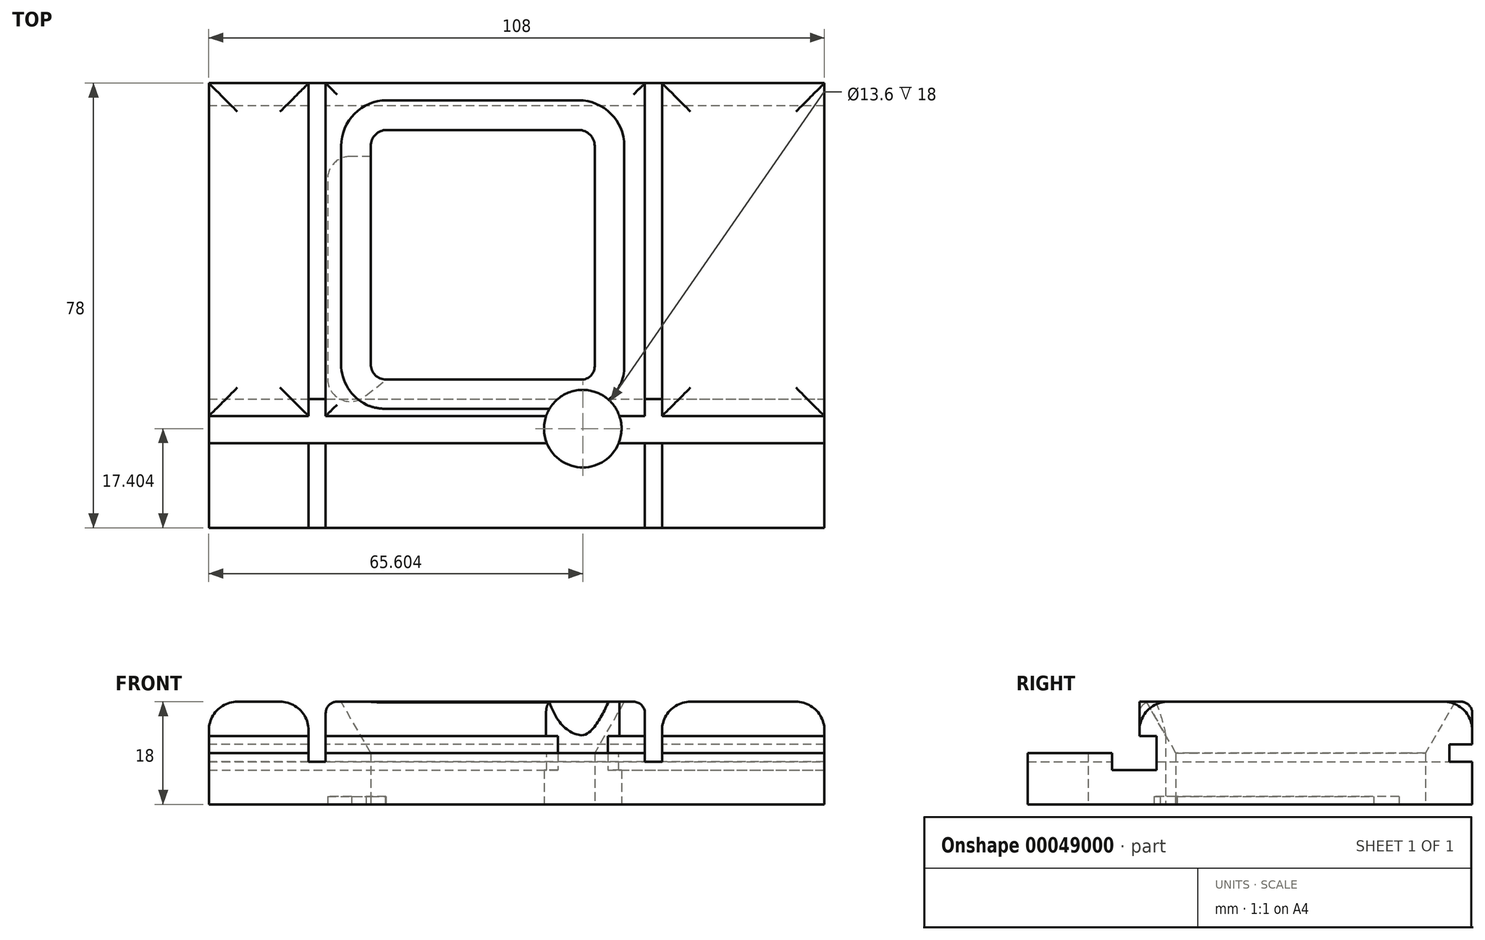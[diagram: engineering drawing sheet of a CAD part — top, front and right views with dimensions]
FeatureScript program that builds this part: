
annotation { "Feature Type Name" : "Feature", "Feature Type Description" : "" }
export const myFeature = defineFeature(function(context is Context, id is Id, definition is map)
    precondition{}
    {
        {
            var Q0;
            Q0=qCreatedBy(makeId("Top.planeOp"),FACE);
            var sketch = newSketch(context, id + "F0", { "sketchPlane" : qUnion([Q0])});
            skLineSegment(sketch, "E0.bottom", {"start": v(-52.02, 49.8) * mm, "end": v(55.98, 49.8) * mm});
            skLineSegment(sketch, "E0.top", {"start": v(-52.02, -28.2) * mm, "end": v(55.98, -28.2) * mm});
            skLineSegment(sketch, "E0.left", {"start": v(-52.02, 49.8) * mm, "end": v(-52.02, -28.2) * mm});
            skLineSegment(sketch, "E0.right", {"start": v(55.98, 49.8) * mm, "end": v(55.98, -28.2) * mm});
            skLineSegment(sketch, "E1", {"start": v(24.48, 49.8) * mm, "end": v(24.48, -28.2) * mm});
            skLineSegment(sketch, "E2", {"start": v(-34.52, 49.8) * mm, "end": v(-34.52, -28.2) * mm});
            skLineSegment(sketch, "E3", {"start": v(-31.52, 49.8) * mm, "end": v(-31.52, -28.2) * mm});
            skLineSegment(sketch, "E4", {"start": v(27.48, 49.8) * mm, "end": v(27.48, -28.2) * mm});
            skLineSegment(sketch, "E5", {"start": v(-52.02, -8.6) * mm, "end": v(55.98, -8.6) * mm});
            skLineSegment(sketch, "E6.bottom", {"start": v(-20.78, 41.6) * mm, "end": v(12.86, 41.6) * mm});
            skLineSegment(sketch, "E6.top", {"start": v(-20.9, -2.2) * mm, "end": v(13.36, -2.2) * mm});
            skLineSegment(sketch, "E6.left", {"start": v(-23.62, 38.77) * mm, "end": v(-23.62, 0.51) * mm});
            skLineSegment(sketch, "E6.right", {"start": v(15.68, 38.78) * mm, "end": v(15.68, 0.13) * mm});
            skCircle(sketch, "E7", {"center": v(13.58, -10.8) * mm, "radius": 6.8 * mm});
            skPoint(sketch, "E8.visualSharp", {"position": v(-23.62, 41.6) * mm});
            skArc(sketch, "E8.filletArc", {"start": v(-20.78, 41.6) * mm, "mid": v(-22.79, 40.77) * mm, "end": v(-23.62, 38.77) * mm});
            skPoint(sketch, "E9.visualSharp", {"position": v(15.68, 41.6) * mm});
            skArc(sketch, "E9.filletArc", {"start": v(15.68, 38.78) * mm, "mid": v(14.86, 40.78) * mm, "end": v(12.86, 41.6) * mm});
            skPoint(sketch, "E10.visualSharp", {"position": v(15.68, -2.2) * mm});
            skArc(sketch, "E10.filletArc", {"start": v(13.36, -2.2) * mm, "mid": v(15, -1.52) * mm, "end": v(15.68, 0.13) * mm});
            skPoint(sketch, "E11.visualSharp", {"position": v(-23.62, -2.2) * mm});
            skArc(sketch, "E11.filletArc", {"start": v(-23.62, 0.51) * mm, "mid": v(-22.82, -1.4) * mm, "end": v(-20.9, -2.2) * mm});
            skSolve(sketch);
        }
        {
            var Q0;
            {var subQ3=sQuery(id+"F0.wireOp",EDGE,"E1");var subQ5=sQuery(id+"F0.wireOp",EDGE,"E0.bottom");var subQ7=makeQuery(id+"F0.imprint","INTERSECT",VERTEX,{"derivedFrom":[subQ5,subQ3]});Q0=makeQuery(id+"F0.imprint","IMPRINT",FACE,{"disambiguationData":[TD([[makeQuery(id+"F0.imprint","IMPRINT",EDGE,{"disambiguationData":[TD([[subQ7,-1.0]])],"derivedFrom":subQ5}),-1.0]])]});}
            var Q1;
            {var subQ3=sQuery(id+"F0.wireOp",EDGE,"E2");var subQ5=sQuery(id+"F0.wireOp",EDGE,"E0.bottom");var subQ7=makeQuery(id+"F0.imprint","INTERSECT",VERTEX,{"derivedFrom":[subQ5,subQ3]});Q1=makeQuery(id+"F0.imprint","IMPRINT",FACE,{"disambiguationData":[TD([[makeQuery(id+"F0.imprint","IMPRINT",EDGE,{"disambiguationData":[TD([[subQ7,-1.0]])],"derivedFrom":subQ5}),-1.0]])]});}
            var Q2;
            {var subQ3=sQuery(id+"F0.wireOp",EDGE,"E0.left");var subQ5=sQuery(id+"F0.wireOp",EDGE,"E0.top");var subQ7=makeQuery(id+"F0.imprint","INTERSECT",VERTEX,{"derivedFrom":[subQ5,subQ3]});Q2=makeQuery(id+"F0.imprint","IMPRINT",FACE,{"disambiguationData":[TD([[makeQuery(id+"F0.imprint","IMPRINT",EDGE,{"disambiguationData":[TD([[subQ7,-1.0]])],"derivedFrom":subQ5}),1.0]])]});}
            var Q3;
            {var subQ3=sQuery(id+"F0.wireOp",EDGE,"E0.right");var subQ5=sQuery(id+"F0.wireOp",EDGE,"E0.top");var subQ7=makeQuery(id+"F0.imprint","INTERSECT",VERTEX,{"derivedFrom":[subQ5,subQ3]});Q3=makeQuery(id+"F0.imprint","IMPRINT",FACE,{"disambiguationData":[TD([[makeQuery(id+"F0.imprint","IMPRINT",EDGE,{"disambiguationData":[TD([[subQ7,1.0]])],"derivedFrom":subQ5}),1.0]])]});}
            var Q4;
            {var subQ3=sQuery(id+"F0.wireOp",EDGE,"E0.left");var subQ5=sQuery(id+"F0.wireOp",EDGE,"E0.bottom");var subQ7=makeQuery(id+"F0.imprint","INTERSECT",VERTEX,{"derivedFrom":[subQ5,subQ3]});Q4=makeQuery(id+"F0.imprint","IMPRINT",FACE,{"disambiguationData":[TD([[makeQuery(id+"F0.imprint","IMPRINT",EDGE,{"disambiguationData":[TD([[subQ7,-1.0]])],"derivedFrom":subQ5}),-1.0]])]});}
            var Q5;
            {var subQ3=sQuery(id+"F0.wireOp",EDGE,"E0.right");var subQ5=sQuery(id+"F0.wireOp",EDGE,"E0.bottom");var subQ7=makeQuery(id+"F0.imprint","INTERSECT",VERTEX,{"derivedFrom":[subQ5,subQ3]});Q5=makeQuery(id+"F0.imprint","IMPRINT",FACE,{"disambiguationData":[TD([[makeQuery(id+"F0.imprint","IMPRINT",EDGE,{"disambiguationData":[TD([[subQ7,1.0]])],"derivedFrom":subQ5}),-1.0]])]});}
            var Q6;
            Q6=makeQuery(id+"F0.imprint","IMPRINT",FACE,{"disambiguationData":[TD([[makeQuery(id+"F0.imprint","IMPRINT",EDGE,{"derivedFrom":sQuery(id+"F0.wireOp",EDGE,"E6.bottom")}),1.0]])]});
            var Q7;
            {var subQ4=sQuery(id+"F0.wireOp",EDGE,"E1");var subQ8=sQuery(id+"F0.wireOp",EDGE,"E0.top");var subQ10=makeQuery(id+"F0.imprint","INTERSECT",VERTEX,{"derivedFrom":[subQ8,subQ4]});Q7=makeQuery(id+"F0.imprint","IMPRINT",FACE,{"disambiguationData":[TD([[makeQuery(id+"F0.imprint","IMPRINT",EDGE,{"disambiguationData":[TD([[subQ10,1.0]])],"derivedFrom":subQ8}),1.0]])]});}
            var Q8;
            {var subQ3=sQuery(id+"F0.wireOp",EDGE,"E1");var subQ5=sQuery(id+"F0.wireOp",EDGE,"E0.top");var subQ7=makeQuery(id+"F0.imprint","INTERSECT",VERTEX,{"derivedFrom":[subQ5,subQ3]});Q8=makeQuery(id+"F0.imprint","IMPRINT",FACE,{"disambiguationData":[TD([[makeQuery(id+"F0.imprint","IMPRINT",EDGE,{"disambiguationData":[TD([[subQ7,-1.0]])],"derivedFrom":subQ5}),1.0]])]});}
            var Q9;
            {var subQ3=sQuery(id+"F0.wireOp",EDGE,"E2");var subQ5=sQuery(id+"F0.wireOp",EDGE,"E0.top");var subQ7=makeQuery(id+"F0.imprint","INTERSECT",VERTEX,{"derivedFrom":[subQ5,subQ3]});Q9=makeQuery(id+"F0.imprint","IMPRINT",FACE,{"disambiguationData":[TD([[makeQuery(id+"F0.imprint","IMPRINT",EDGE,{"disambiguationData":[TD([[subQ7,-1.0]])],"derivedFrom":subQ5}),1.0]])]});}
            extrude(context, id + "F1", {"entities" : qUnion([Q0, Q1, Q2, Q3, Q4, Q5, Q6, Q7, Q8, Q9]), "depth" : 7.5 * mm});
        }
        {
            var Q0;
            {var subQ3=sQuery(id+"F0.wireOp",EDGE,"E0.left");var subQ5=sQuery(id+"F0.wireOp",EDGE,"E0.bottom");var subQ7=makeQuery(id+"F0.imprint","INTERSECT",VERTEX,{"derivedFrom":[subQ5,subQ3]});Q0=makeQuery(id+"F0.imprint","IMPRINT",FACE,{"disambiguationData":[TD([[makeQuery(id+"F0.imprint","IMPRINT",EDGE,{"disambiguationData":[TD([[subQ7,-1.0]])],"derivedFrom":subQ5}),-1.0]])]});}
            var Q1;
            {var subQ3=sQuery(id+"F0.wireOp",EDGE,"E0.left");var subQ5=sQuery(id+"F0.wireOp",EDGE,"E0.top");var subQ7=makeQuery(id+"F0.imprint","INTERSECT",VERTEX,{"derivedFrom":[subQ5,subQ3]});Q1=makeQuery(id+"F0.imprint","IMPRINT",FACE,{"disambiguationData":[TD([[makeQuery(id+"F0.imprint","IMPRINT",EDGE,{"disambiguationData":[TD([[subQ7,-1.0]])],"derivedFrom":subQ5}),1.0]])]});}
            var Q2;
            {var subQ4=sQuery(id+"F0.wireOp",EDGE,"E1");var subQ8=sQuery(id+"F0.wireOp",EDGE,"E0.top");var subQ10=makeQuery(id+"F0.imprint","INTERSECT",VERTEX,{"derivedFrom":[subQ8,subQ4]});Q2=makeQuery(id+"F0.imprint","IMPRINT",FACE,{"disambiguationData":[TD([[makeQuery(id+"F0.imprint","IMPRINT",EDGE,{"disambiguationData":[TD([[subQ10,1.0]])],"derivedFrom":subQ8}),1.0]])]});}
            var Q3;
            Q3=makeQuery(id+"F0.imprint","IMPRINT",FACE,{"disambiguationData":[TD([[makeQuery(id+"F0.imprint","IMPRINT",EDGE,{"derivedFrom":sQuery(id+"F0.wireOp",EDGE,"E6.bottom")}),1.0]])]});
            var Q4;
            {var subQ3=sQuery(id+"F0.wireOp",EDGE,"E0.right");var subQ5=sQuery(id+"F0.wireOp",EDGE,"E0.bottom");var subQ7=makeQuery(id+"F0.imprint","INTERSECT",VERTEX,{"derivedFrom":[subQ5,subQ3]});Q4=makeQuery(id+"F0.imprint","IMPRINT",FACE,{"disambiguationData":[TD([[makeQuery(id+"F0.imprint","IMPRINT",EDGE,{"disambiguationData":[TD([[subQ7,1.0]])],"derivedFrom":subQ5}),-1.0]])]});}
            var Q5;
            {var subQ3=sQuery(id+"F0.wireOp",EDGE,"E0.right");var subQ5=sQuery(id+"F0.wireOp",EDGE,"E0.top");var subQ7=makeQuery(id+"F0.imprint","INTERSECT",VERTEX,{"derivedFrom":[subQ5,subQ3]});Q5=makeQuery(id+"F0.imprint","IMPRINT",FACE,{"disambiguationData":[TD([[makeQuery(id+"F0.imprint","IMPRINT",EDGE,{"disambiguationData":[TD([[subQ7,1.0]])],"derivedFrom":subQ5}),1.0]])]});}
            extrude(context, id + "F2", {"entities" : qUnion([Q0, Q1, Q2, Q3, Q4, Q5]), "operationType" : NewBodyOperationType.ADD, "depth" : 9 * mm});
        }
        {
            var Q0;
            {var subQ3=sQuery(id+"F0.wireOp",EDGE,"E0.left");var subQ5=sQuery(id+"F0.wireOp",EDGE,"E0.bottom");var subQ7=makeQuery(id+"F0.imprint","INTERSECT",VERTEX,{"derivedFrom":[subQ5,subQ3]});Q0=makeQuery(id+"F0.imprint","IMPRINT",FACE,{"disambiguationData":[TD([[makeQuery(id+"F0.imprint","IMPRINT",EDGE,{"disambiguationData":[TD([[subQ7,-1.0]])],"derivedFrom":subQ5}),-1.0]])]});}
            var Q1;
            Q1=makeQuery(id+"F0.imprint","IMPRINT",FACE,{"disambiguationData":[TD([[makeQuery(id+"F0.imprint","IMPRINT",EDGE,{"derivedFrom":sQuery(id+"F0.wireOp",EDGE,"E6.bottom")}),1.0]])]});
            var Q2;
            {var subQ3=sQuery(id+"F0.wireOp",EDGE,"E0.right");var subQ5=sQuery(id+"F0.wireOp",EDGE,"E0.bottom");var subQ7=makeQuery(id+"F0.imprint","INTERSECT",VERTEX,{"derivedFrom":[subQ5,subQ3]});Q2=makeQuery(id+"F0.imprint","IMPRINT",FACE,{"disambiguationData":[TD([[makeQuery(id+"F0.imprint","IMPRINT",EDGE,{"disambiguationData":[TD([[subQ7,1.0]])],"derivedFrom":subQ5}),-1.0]])]});}
            extrude(context, id + "F3", {"entities" : qUnion([Q0, Q1, Q2]), "operationType" : NewBodyOperationType.ADD, "depth" : 18 * mm});
        }
        {
            var Q0;
            Q0=makeQuery(id+"F3.opExtrude","CAP_FACE",FACE,{"disambiguationData":[OSD([sQuery(id+"F0.wireOp",EDGE,"E0.bottom"),sQuery(id+"F0.wireOp",EDGE,"E0.right"),sQuery(id+"F0.wireOp",EDGE,"E4"),sQuery(id+"F0.wireOp",EDGE,"E5")])],"isStart":false});
            fillet(context, id + "F4", {"entities" : qUnion([Q0]), "radius" : 5 * mm, "tangentPropagation" : true, "allowEdgeOverflow" : false});
        }
        {
            var Q0;
            Q0=makeQuery(id+"F3.opExtrude","CAP_FACE",FACE,{"disambiguationData":[OSD([sQuery(id+"F0.wireOp",EDGE,"E0.bottom"),sQuery(id+"F0.wireOp",EDGE,"E0.left"),sQuery(id+"F0.wireOp",EDGE,"E2"),sQuery(id+"F0.wireOp",EDGE,"E5")])],"isStart":false});
            fillet(context, id + "F5", {"entities" : qUnion([Q0]), "radius" : 5 * mm, "tangentPropagation" : true, "allowEdgeOverflow" : false});
        }
        {
            var Q0;
            Q0=makeQuery(id+"F3.opExtrude","CAP_EDGE",EDGE,{"disambiguationData":[OSD([sQuery(id+"F0.wireOp",EDGE,"E6.left")])],"isStart":false});
            var Q1;
            Q1=makeQuery(id+"F3.opExtrude","CAP_EDGE",EDGE,{"disambiguationData":[OSD([sQuery(id+"F0.wireOp",EDGE,"E6.bottom")])],"isStart":false});
            var Q2;
            Q2=makeQuery(id+"F3.opExtrude","CAP_EDGE",EDGE,{"disambiguationData":[OSD([sQuery(id+"F0.wireOp",EDGE,"E6.right")])],"isStart":false});
            var Q3;
            Q3=makeQuery(id+"F3.opExtrude","CAP_EDGE",EDGE,{"disambiguationData":[OSD([sQuery(id+"F0.wireOp",EDGE,"E6.top")])],"isStart":false});
            chamfer(context, id + "F6", {"entities" : qUnion([Q0, Q1, Q2, Q3]), "chamferType" : ChamferType.OFFSET_ANGLE, "width" : 9 * mm, "oppositeDirection" : false, "angle" : 30 * degree, "tangentPropagation" : true});
        }
        {
            var Q0;
            Q0=makeQuery(id+"F3.opExtrude","CAP_EDGE",EDGE,{"disambiguationData":[OSD([sQuery(id+"F0.wireOp",EDGE,"E3")])],"isStart":false});
            var Q1;
            {var subQ0=sQuery(id+"F0.wireOp",EDGE,"E0.bottom");Q1=makeQuery(id+"F3.opExtrude","CAP_EDGE",EDGE,{"disambiguationData":[OSD([subQ0]),TDD([makeQuery(id+"F0.imprint","IMPRINT",EDGE,{"disambiguationData":[TD([[makeQuery(id+"F0.imprint","INTERSECT",VERTEX,{"derivedFrom":[subQ0,sQuery(id+"F0.wireOp",EDGE,"E1")]}),1.0]])],"derivedFrom":subQ0})])],"isStart":false});}
            var Q2;
            Q2=makeQuery(id+"F3.opExtrude","CAP_EDGE",EDGE,{"disambiguationData":[OSD([sQuery(id+"F0.wireOp",EDGE,"E1")])],"isStart":false});
            var Q3;
            {var subQ0=sQuery(id+"F0.wireOp",EDGE,"E5");Q3=makeQuery(id+"F3.opExtrude","CAP_EDGE",EDGE,{"disambiguationData":[OSD([subQ0]),TDD([makeQuery(id+"F0.imprint","IMPRINT",EDGE,{"disambiguationData":[TD([[makeQuery(id+"F0.imprint","INTERSECT",VERTEX,{"derivedFrom":[sQuery(id+"F0.wireOp",EDGE,"E3"),subQ0]}),-1.0]])],"derivedFrom":subQ0})])],"isStart":false});}
            fillet(context, id + "F7", {"entities" : qUnion([Q0, Q1, Q2, Q3]), "radius" : 2 * mm, "tangentPropagation" : true, "allowEdgeOverflow" : false});
        }
        {
            var Q0;
            {var subQ0=sQuery(id+"F0.wireOp",EDGE,"E0.bottom");var subQ1=makeQuery(id+"F0.imprint","IMPRINT",EDGE,{"disambiguationData":[TD([[makeQuery(id+"F0.imprint","INTERSECT",VERTEX,{"derivedFrom":[subQ0,sQuery(id+"F0.wireOp",EDGE,"E0.left")]}),-1.0]])],"derivedFrom":subQ0});var subQ2=makeQuery(id+"F0.imprint","IMPRINT",EDGE,{"disambiguationData":[TD([[makeQuery(id+"F0.imprint","INTERSECT",VERTEX,{"derivedFrom":[subQ0,sQuery(id+"F0.wireOp",EDGE,"E1")]}),1.0]])],"derivedFrom":subQ0});var subQ3=makeQuery(id+"F0.imprint","IMPRINT",EDGE,{"disambiguationData":[TD([[makeQuery(id+"F0.imprint","INTERSECT",VERTEX,{"derivedFrom":[subQ0,sQuery(id+"F0.wireOp",EDGE,"E0.right")]}),1.0]])],"derivedFrom":subQ0});Q0=makeQuery(id+"F3.boolean.opBoolean","MERGE",FACE,{"derivedFrom":[makeQuery(id+"F2.boolean.opBoolean","MERGE",FACE,{"derivedFrom":[makeQuery(id+"F1.opExtrude","SWEPT_FACE",FACE,{"disambiguationData":[OSD([subQ0])]}),makeQuery(id+"F2.opExtrude","SWEPT_FACE",FACE,{"disambiguationData":[OSD([subQ0]),TDD([subQ1])]}),makeQuery(id+"F2.opExtrude","SWEPT_FACE",FACE,{"disambiguationData":[OSD([subQ0]),TDD([subQ2])]}),makeQuery(id+"F2.opExtrude","SWEPT_FACE",FACE,{"disambiguationData":[OSD([subQ0]),TDD([subQ3])]})]}),makeQuery(id+"F3.opExtrude","SWEPT_FACE",FACE,{"disambiguationData":[OSD([subQ0]),TDD([subQ1])]}),makeQuery(id+"F3.opExtrude","SWEPT_FACE",FACE,{"disambiguationData":[OSD([subQ0]),TDD([subQ2])]}),makeQuery(id+"F3.opExtrude","SWEPT_FACE",FACE,{"disambiguationData":[OSD([subQ0]),TDD([subQ3])]})]});}
            var sketch = newSketch(context, id + "F8", { "sketchPlane" : qUnion([Q0])});
            skLineSegment(sketch, "E12.bottom", {"start": v(-55.98, 7.5) * mm, "end": v(52.02, 7.5) * mm});
            skLineSegment(sketch, "E12.top", {"start": v(-55.98, 10.5) * mm, "end": v(52.02, 10.5) * mm});
            skLineSegment(sketch, "E12.left", {"start": v(-55.98, 7.5) * mm, "end": v(-55.98, 10.5) * mm});
            skLineSegment(sketch, "E12.right", {"start": v(52.02, 7.5) * mm, "end": v(52.02, 10.5) * mm});
            skSolve(sketch);
        }
        {
            var Q0;
            {var subQ0=sQuery(id+"F0.wireOp",EDGE,"E0.bottom");var subQ1=sQuery(id+"F0.wireOp",EDGE,"E3");var subQ2=makeQuery(id+"F3.boolean.opBoolean","MERGE",EDGE,{"derivedFrom":[makeQuery(id+"F2.opExtrude","SWEPT_EDGE",EDGE,{"disambiguationData":[OSD([subQ0,subQ1])]}),makeQuery(id+"F3.opExtrude","SWEPT_EDGE",EDGE,{"disambiguationData":[OSD([subQ0,subQ1])]})]});var subQ5=sQuery(id+"F8.wireOp",EDGE,"E12.bottom");var subQ6=makeQuery(id+"F8.imprint","INTERSECT",VERTEX,{"derivedFrom":[subQ2,subQ5]});var subQ7=sQuery(id+"F0.wireOp",EDGE,"E1");var subQ8=makeQuery(id+"F3.boolean.opBoolean","MERGE",EDGE,{"derivedFrom":[makeQuery(id+"F2.opExtrude","SWEPT_EDGE",EDGE,{"disambiguationData":[OSD([subQ0,subQ7])]}),makeQuery(id+"F3.opExtrude","SWEPT_EDGE",EDGE,{"disambiguationData":[OSD([subQ0,subQ7])]})]});var subQ10=makeQuery(id+"F8.imprint","INTERSECT",VERTEX,{"derivedFrom":[subQ8,subQ5]});Q0=makeQuery(id+"F8.imprint","IMPRINT",FACE,{"disambiguationData":[TD([[makeQuery(id+"F8.imprint","IMPRINT",EDGE,{"disambiguationData":[TD([[subQ10,-1.0],[subQ6,1.0]])],"derivedFrom":subQ5}),1.0]])]});}
            var Q1;
            {var subQ7=sQuery(id+"F8.wireOp",EDGE,"E12.left");Q1=makeQuery(id+"F8.imprint","IMPRINT",FACE,{"disambiguationData":[TD([[makeQuery(id+"F8.imprint","IMPRINT",EDGE,{"derivedFrom":subQ7}),1.0]])]});}
            var Q2;
            {var subQ7=sQuery(id+"F8.wireOp",EDGE,"E12.right");Q2=makeQuery(id+"F8.imprint","IMPRINT",FACE,{"disambiguationData":[TD([[makeQuery(id+"F8.imprint","IMPRINT",EDGE,{"derivedFrom":subQ7}),-1.0]])]});}
            extrude(context, id + "F9", {"entities" : qUnion([Q0, Q1, Q2]), "operationType" : NewBodyOperationType.REMOVE, "oppositeDirection" : true, "depth" : 4 * mm});
        }
        {
            var Q0;
            {var subQ0=sQuery(id+"F0.wireOp",EDGE,"E5");Q0=makeQuery(id+"F3.opExtrude","SWEPT_FACE",FACE,{"disambiguationData":[OSD([subQ0]),TDD([makeQuery(id+"F0.imprint","IMPRINT",EDGE,{"disambiguationData":[TD([[makeQuery(id+"F0.imprint","INTERSECT",VERTEX,{"derivedFrom":[sQuery(id+"F0.wireOp",EDGE,"E3"),subQ0]}),-1.0]])],"derivedFrom":subQ0})])]});}
            var sketch = newSketch(context, id + "F10", { "sketchPlane" : qUnion([Q0])});
            skLineSegment(sketch, "E13.bottom", {"start": v(-52.82, 9) * mm, "end": v(58.8, 9) * mm});
            skLineSegment(sketch, "E13.top", {"start": v(-52.82, 12) * mm, "end": v(58.8, 12) * mm});
            skLineSegment(sketch, "E13.left", {"start": v(-52.82, 9) * mm, "end": v(-52.82, 12) * mm});
            skLineSegment(sketch, "E13.right", {"start": v(58.8, 9) * mm, "end": v(58.8, 12) * mm});
            skSolve(sketch);
        }
        {
            var Q0;
            {var subQ5=sQuery(id+"F10.wireOp",EDGE,"E13.left");Q0=makeQuery(id+"F10.imprint","IMPRINT",FACE,{"disambiguationData":[TD([[makeQuery(id+"F10.imprint","IMPRINT",EDGE,{"derivedFrom":subQ5}),-1.0]])]});}
            var Q1;
            {var subQ0=sQuery(id+"F0.wireOp",EDGE,"E5");var subQ1=sQuery(id+"F0.wireOp",EDGE,"E7");var subQ2=makeQuery(id+"F3.opExtrude","SWEPT_EDGE",EDGE,{"disambiguationData":[OSD([subQ0,subQ1]),TDD([makeQuery(id+"F0.imprint","INTERSECT",VERTEX,{"disambiguationData":[OD(0.0)],"derivedFrom":[subQ0,subQ1]})])]});var subQ5=sQuery(id+"F10.wireOp",EDGE,"E13.bottom");var subQ6=makeQuery(id+"F10.imprint","INTERSECT",VERTEX,{"derivedFrom":[subQ2,subQ5]});var subQ7=makeQuery(id+"F3.opExtrude","SWEPT_EDGE",EDGE,{"disambiguationData":[OSD([sQuery(id+"F0.wireOp",EDGE,"E3"),subQ0])]});var subQ9=makeQuery(id+"F10.imprint","INTERSECT",VERTEX,{"derivedFrom":[subQ7,subQ5]});Q1=makeQuery(id+"F10.imprint","IMPRINT",FACE,{"disambiguationData":[TD([[makeQuery(id+"F10.imprint","IMPRINT",EDGE,{"disambiguationData":[TD([[subQ9,1.0],[subQ6,-1.0]])],"derivedFrom":subQ5}),-1.0]])]});}
            var Q2;
            {var subQ7=sQuery(id+"F10.wireOp",EDGE,"E13.right");Q2=makeQuery(id+"F10.imprint","IMPRINT",FACE,{"disambiguationData":[TD([[makeQuery(id+"F10.imprint","IMPRINT",EDGE,{"derivedFrom":subQ7}),1.0]])]});}
            extrude(context, id + "F11", {"entities" : qUnion([Q0, Q1, Q2]), "operationType" : NewBodyOperationType.REMOVE, "oppositeDirection" : true, "depth" : 3 * mm});
        }
        {
            var Q0;
            Q0=makeQuery(id+"F11.boolean.opBoolean","MERGE",FACE,{"derivedFrom":[makeQuery(id+"F2.opExtrude","CAP_FACE",FACE,{"disambiguationData":[OSD([sQuery(id+"F0.wireOp",EDGE,"E0.bottom"),sQuery(id+"F0.wireOp",EDGE,"E0.top"),sQuery(id+"F0.wireOp",EDGE,"E1"),sQuery(id+"F0.wireOp",EDGE,"E3"),sQuery(id+"F0.wireOp",EDGE,"E6.bottom"),sQuery(id+"F0.wireOp",EDGE,"E6.top"),sQuery(id+"F0.wireOp",EDGE,"E6.left"),sQuery(id+"F0.wireOp",EDGE,"E6.right"),sQuery(id+"F0.wireOp",EDGE,"E7"),sQuery(id+"F0.wireOp",EDGE,"E8.filletArc"),sQuery(id+"F0.wireOp",EDGE,"E9.filletArc"),sQuery(id+"F0.wireOp",EDGE,"E10.filletArc"),sQuery(id+"F0.wireOp",EDGE,"E11.filletArc")])],"isStart":false}),makeQuery(id+"F11.opExtrude","SWEPT_FACE",FACE,{"disambiguationData":[OSD([sQuery(id+"F10.wireOp",EDGE,"E13.bottom")])]})]});
            var sketch = newSketch(context, id + "F12", { "sketchPlane" : qUnion([Q0])});
            skLineSegment(sketch, "E14.bottom", {"start": v(-60.93, -5.6) * mm, "end": v(56.85, -5.6) * mm});
            skLineSegment(sketch, "E14.top", {"start": v(-60.93, -13.37) * mm, "end": v(56.85, -13.37) * mm});
            skLineSegment(sketch, "E14.left", {"start": v(-60.93, -5.6) * mm, "end": v(-60.93, -13.37) * mm});
            skLineSegment(sketch, "E14.right", {"start": v(56.85, -5.6) * mm, "end": v(56.85, -13.37) * mm});
            skSolve(sketch);
        }
        {
            var Q0;
            {var subQ1=makeQuery(id+"F11.opExtrude","SWEPT_FACE",FACE,{"disambiguationData":[OSD([sQuery(id+"F10.wireOp",EDGE,"E13.bottom")])]});var subQ5=sQuery(id+"F12.wireOp",EDGE,"E14.bottom");var subQ7=sQuery(id+"F0.wireOp",EDGE,"E3");var subQ8=makeQuery(id+"F11.boolean.opBoolean","INTERSECT",EDGE,{"derivedFrom":[makeQuery(id+"F3.boolean.opBoolean","MERGE",FACE,{"derivedFrom":[makeQuery(id+"F2.opExtrude","SWEPT_FACE",FACE,{"disambiguationData":[OSD([subQ7])]}),makeQuery(id+"F3.opExtrude","SWEPT_FACE",FACE,{"disambiguationData":[OSD([subQ7])]})]}),subQ1]});var subQ10=makeQuery(id+"F12.imprint","INTERSECT",VERTEX,{"derivedFrom":[subQ8,subQ5]});Q0=makeQuery(id+"F12.imprint","IMPRINT",FACE,{"disambiguationData":[TD([[makeQuery(id+"F12.imprint","IMPRINT",EDGE,{"disambiguationData":[TD([[subQ10,-1.0]])],"derivedFrom":subQ5}),-1.0]])]});}
            var Q1;
            {var subQ6=sQuery(id+"F12.wireOp",EDGE,"E14.left");Q1=makeQuery(id+"F12.imprint","IMPRINT",FACE,{"disambiguationData":[TD([[makeQuery(id+"F12.imprint","IMPRINT",EDGE,{"derivedFrom":subQ6}),1.0]])]});}
            var Q2;
            {var subQ1=makeQuery(id+"F11.opExtrude","SWEPT_FACE",FACE,{"disambiguationData":[OSD([sQuery(id+"F10.wireOp",EDGE,"E13.bottom")])]});var subQ5=sQuery(id+"F12.wireOp",EDGE,"E14.bottom");var subQ7=sQuery(id+"F0.wireOp",EDGE,"E1");var subQ8=makeQuery(id+"F11.boolean.opBoolean","INTERSECT",EDGE,{"derivedFrom":[makeQuery(id+"F3.boolean.opBoolean","MERGE",FACE,{"derivedFrom":[makeQuery(id+"F2.opExtrude","SWEPT_FACE",FACE,{"disambiguationData":[OSD([subQ7])]}),makeQuery(id+"F3.opExtrude","SWEPT_FACE",FACE,{"disambiguationData":[OSD([subQ7])]})]}),subQ1]});var subQ10=makeQuery(id+"F12.imprint","INTERSECT",VERTEX,{"derivedFrom":[subQ8,subQ5]});Q2=makeQuery(id+"F12.imprint","IMPRINT",FACE,{"disambiguationData":[TD([[makeQuery(id+"F12.imprint","IMPRINT",EDGE,{"disambiguationData":[TD([[subQ10,1.0]])],"derivedFrom":subQ5}),-1.0]])]});}
            var Q3;
            {var subQ6=sQuery(id+"F12.wireOp",EDGE,"E14.right");Q3=makeQuery(id+"F12.imprint","IMPRINT",FACE,{"disambiguationData":[TD([[makeQuery(id+"F12.imprint","IMPRINT",EDGE,{"derivedFrom":subQ6}),-1.0]])]});}
            extrude(context, id + "F13", {"entities" : qUnion([Q0, Q1, Q2, Q3]), "operationType" : NewBodyOperationType.REMOVE, "oppositeDirection" : true, "depth" : 3 * mm});
        }
        {
            var Q0;
            Q0=makeQuery(id+"F0.imprint","IMPRINT",FACE,{"disambiguationData":[TD([[makeQuery(id+"F0.imprint","IMPRINT",EDGE,{"derivedFrom":sQuery(id+"F0.wireOp",EDGE,"E6.bottom")}),1.0]])]});
            var sketch = newSketch(context, id + "F14", { "sketchPlane" : qUnion([Q0])});
            skCircle(sketch, "E15", {"center": v(-27.18, -2.04) * mm, "radius": 4 * mm});
            skCircle(sketch, "E16", {"center": v(-27.18, 32.96) * mm, "radius": 4 * mm});
            skLineSegment(sketch, "E17.bottom", {"start": v(-31.18, -1.97) * mm, "end": v(-23.2, -1.97) * mm});
            skLineSegment(sketch, "E17.top", {"start": v(-31.18, 32.54) * mm, "end": v(-23.2, 32.54) * mm});
            skLineSegment(sketch, "E17.left", {"start": v(-31.18, -1.97) * mm, "end": v(-31.18, 32.54) * mm});
            skLineSegment(sketch, "E17.right", {"start": v(-23.2, -1.97) * mm, "end": v(-23.2, 32.54) * mm});
            skLineSegment(sketch, "E18", {"start": v(-20.95, -2.28) * mm, "end": v(-23.2, 0) * mm});
            skLineSegment(sketch, "E19", {"start": v(-26.98, 36.96) * mm, "end": v(-22.03, 36.96) * mm});
            skLineSegment(sketch, "E20", {"start": v(-22.03, 36.96) * mm, "end": v(-23.2, 32.54) * mm});
            skLineSegment(sketch, "E21", {"start": v(-20.95, -2.28) * mm, "end": v(-25.1, -5.45) * mm});
            skSolve(sketch);
        }
        {
            var Q0;
            {var subQ3=sQuery(id+"F14.wireOp",EDGE,"E17.bottom");Q0=makeQuery(id+"F14.imprint","IMPRINT",FACE,{"disambiguationData":[TD([[makeQuery(id+"F14.imprint","IMPRINT",EDGE,{"derivedFrom":subQ3}),-1.0]])]});}
            var Q1;
            {var subQ3=sQuery(id+"F14.wireOp",EDGE,"E17.bottom");Q1=makeQuery(id+"F14.imprint","IMPRINT",FACE,{"disambiguationData":[TD([[makeQuery(id+"F14.imprint","IMPRINT",EDGE,{"derivedFrom":subQ3}),1.0]])]});}
            var Q2;
            {var subQ9=sQuery(id+"F14.wireOp",EDGE,"E17.left");Q2=makeQuery(id+"F14.imprint","IMPRINT",FACE,{"disambiguationData":[TD([[makeQuery(id+"F14.imprint","IMPRINT",EDGE,{"derivedFrom":subQ9}),-1.0]])]});}
            var Q3;
            {var subQ1=sQuery(id+"F14.wireOp",EDGE,"E17.top");var subQ3=sQuery(id+"F14.wireOp",EDGE,"E16");var subQ5=makeQuery(id+"F14.imprint","INTERSECT",VERTEX,{"derivedFrom":[subQ3,subQ1]});Q3=makeQuery(id+"F14.imprint","IMPRINT",FACE,{"disambiguationData":[TD([[makeQuery(id+"F14.imprint","IMPRINT",EDGE,{"disambiguationData":[TD([[subQ5,-1.0]])],"derivedFrom":subQ3}),1.0]])]});}
            var Q4;
            {var subQ1=sQuery(id+"F14.wireOp",EDGE,"E17.top");var subQ3=sQuery(id+"F14.wireOp",EDGE,"E16");var subQ5=makeQuery(id+"F14.imprint","INTERSECT",VERTEX,{"derivedFrom":[subQ3,subQ1]});Q4=makeQuery(id+"F14.imprint","IMPRINT",FACE,{"disambiguationData":[TD([[makeQuery(id+"F14.imprint","IMPRINT",EDGE,{"disambiguationData":[TD([[subQ5,1.0]])],"derivedFrom":subQ3}),1.0]])]});}
            var Q5;
            {var subQ0=sQuery(id+"F14.wireOp",EDGE,"f461685c-614d-4517-aff4-d02b1853712a");var subQ1=sQuery(id+"F14.wireOp",EDGE,"E15");var subQ3=makeQuery(id+"F14.imprint","INTERSECT",VERTEX,{"disambiguationData":[OD(0.0)],"derivedFrom":[subQ1,subQ0]});Q5=makeQuery(id+"F14.imprint","IMPRINT",FACE,{"disambiguationData":[TD([[makeQuery(id+"F14.imprint","IMPRINT",EDGE,{"disambiguationData":[TD([[subQ3,-1.0]])],"derivedFrom":subQ1}),1.0]])]});}
            var Q6;
            {var subQ3=sQuery(id+"F14.wireOp",EDGE,"E17.right");var subQ7=sQuery(id+"F14.wireOp",EDGE,"E15");var subQ9=makeQuery(id+"F14.imprint","INTERSECT",VERTEX,{"derivedFrom":[subQ7,subQ3]});Q6=makeQuery(id+"F14.imprint","IMPRINT",FACE,{"disambiguationData":[TD([[makeQuery(id+"F14.imprint","IMPRINT",EDGE,{"disambiguationData":[TD([[subQ9,1.0]])],"derivedFrom":subQ7}),-1.0]])]});}
            var Q7;
            {var subQ1=sQuery(id+"F14.wireOp",EDGE,"E19");var subQ3=sQuery(id+"F14.wireOp",EDGE,"E16");var subQ5=makeQuery(id+"F14.imprint","INTERSECT",VERTEX,{"derivedFrom":[subQ3,subQ1]});Q7=makeQuery(id+"F14.imprint","IMPRINT",FACE,{"disambiguationData":[TD([[makeQuery(id+"F14.imprint","IMPRINT",EDGE,{"disambiguationData":[TD([[subQ5,1.0]])],"derivedFrom":subQ3}),-1.0]])]});}
            extrude(context, id + "F15", {"entities" : qUnion([Q0, Q1, Q2, Q3, Q4, Q5, Q6, Q7]), "operationType" : NewBodyOperationType.REMOVE, "endBound" : BoundingType.SYMMETRIC, "depth" : 2.7 * mm});
        }
    });
